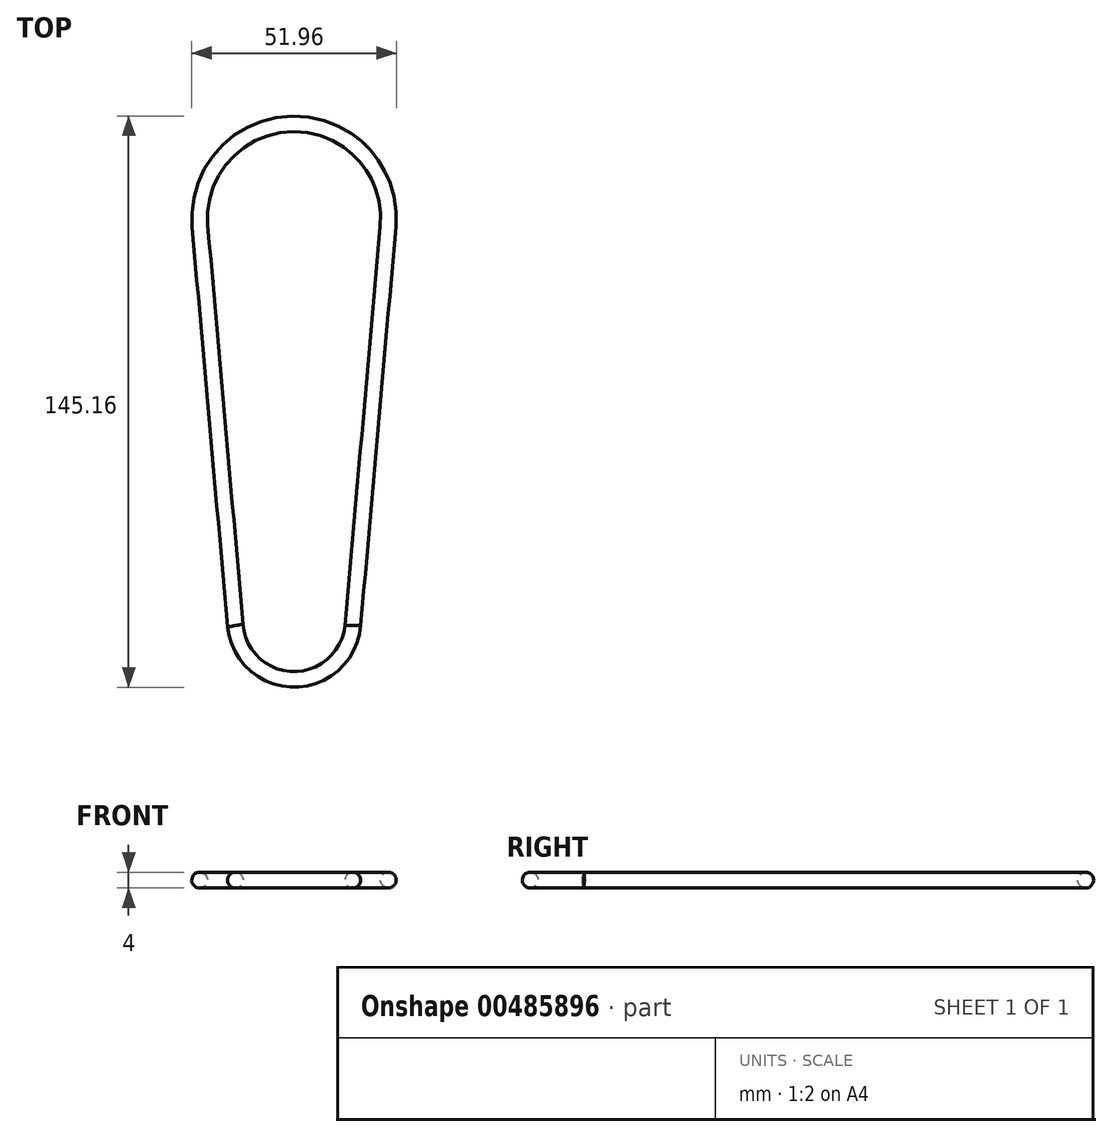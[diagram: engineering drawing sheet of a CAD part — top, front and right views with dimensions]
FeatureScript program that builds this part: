
annotation { "Feature Type Name" : "Feature", "Feature Type Description" : "" }
export const myFeature = defineFeature(function(context is Context, id is Id, definition is map)
    precondition{}
    {
        {
            var Q0;
            Q0=qCreatedBy(makeId("Top.planeOp"),FACE);
            var sketch = newSketch(context, id + "F0", { "sketchPlane" : qUnion([Q0])});
            skArc(sketch, "E0", {"start": v(23.9, -2.11) * mm, "mid": v(0, 24) * mm, "end": v(-23.9, -2.11) * mm});
            skLineSegment(sketch, "E1", {"start": v(0, 0) * mm, "end": v(0, -102.2) * mm, "construction": true});
            skArc(sketch, "E2", {"start": v(-14.94, -103.52) * mm, "mid": v(0, -117.2) * mm, "end": v(14.94, -103.52) * mm});
            skLineSegment(sketch, "E3", {"start": v(23.9, -2.11) * mm, "end": v(14.94, -103.52) * mm});
            skLineSegment(sketch, "E4", {"start": v(-23.9, -2.11) * mm, "end": v(-14.94, -103.52) * mm});
            skSolve(sketch);
        }
        {
            var Q0;
            Q0=qCreatedBy(makeId("Front.planeOp"),FACE);
            cPlane(context, id + "F1", {"entities" : qUnion([Q0]), "cplaneType" : CPlaneType.OFFSET, "offset" : 1.96 * mm, "width" : 150 * mm, "height" : 150 * mm});
        }
        {
            var Q0;
            Q0=qCreatedBy(id+"F1.planeOp",FACE);
            var sketch = newSketch(context, id + "F2", { "sketchPlane" : qUnion([Q0])});
            skPoint(sketch, "E5.0", {"position": v(23.9, 0) * mm});
            skCircle(sketch, "E6", {"center": v(23.9, 0) * mm, "radius": 2 * mm});
            skSolve(sketch);
        }
        {
            var Q0;
            Q0=makeQuery(id+"F2.imprint","IMPRINT",FACE,{"disambiguationData":[TD([[makeQuery(id+"F2.imprint","IMPRINT",EDGE,{"derivedFrom":sQuery(id+"F2.wireOp",EDGE,"E6")}),1.0]])]});
            var Q1;
            Q1=sQuery(id+"F0.wireOp",EDGE,"E3");
            var Q2;
            Q2=sQuery(id+"F0.wireOp",EDGE,"E2");
            var Q3;
            Q3=sQuery(id+"F0.wireOp",EDGE,"E4");
            var Q4;
            Q4=sQuery(id+"F0.wireOp",EDGE,"E0");
            sweep(context, id + "F3", {"profiles" : qUnion([Q0]), "path" : qUnion([Q1, Q2, Q3, Q4])});
        }
    });
